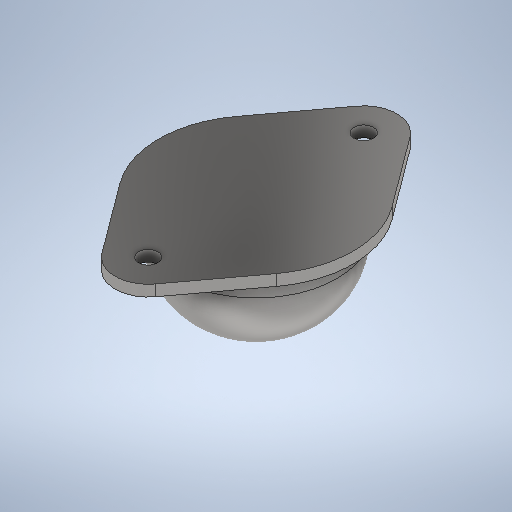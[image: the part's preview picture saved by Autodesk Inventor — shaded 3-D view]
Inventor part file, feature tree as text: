
AUTODESK INVENTOR PART (.ipt)
format: ipt  version: 2025 (Build 290162000, 162)  size: 290,816 bytes
history: native  units: mm
features: extrude x2, sketch x2, fillet x1
ambient origin geometry x8: Origin, YZ Plane, XZ Plane, XY Plane, X Axis, Y Axis, Z Axis, Center Point
bodies: Solide1 (feature_tree)
feature tree (5):
  extrude  "Extrusion1"  Depth=3.5mm
  extrude  "Extrusion2"  Depth=35.0mm
  fillet  "Congé1"  Radius=19.4mm
  sketch  "Esquisse1"
  sketch  "Esquisse2"
